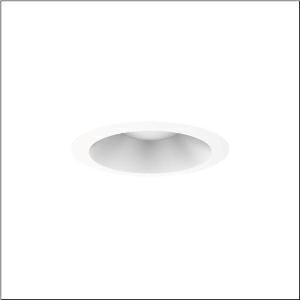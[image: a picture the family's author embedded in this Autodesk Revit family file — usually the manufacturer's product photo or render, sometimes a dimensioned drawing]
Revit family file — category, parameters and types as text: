
# Revit family: lunis_31_midi_51dn16dg32
name_source: partatom
category: Lighting Fixtures
units: mm (PartAtom-declared; Revit-internal decimal feet)

## family parameters
Cut with Voids When Loaded = No
Host = Face
Light Source = No
Part Type = Normal
Room Calculation Point = No
Round Connector Dimension = Use Diameter
Shared = No

## types (1)
- Lunis 31 midi (1 x LED, 2000 lm, 17 W, 3000K)
    Apparent Load = 17 VA
    CIE Flux Codes = 64 93 99 100 100
    Color Rendering = 80
    Color Temperature = 3000K
    Default Elevation = 1800 mm
    Description = Lunis 31,  midi, downlight, light control with reflector, light emission: direct distribution, LED rated luminous flux: 2.000lm, light colour: 830, mains connection: 220..240V, AC, 50/60Hz, housing, white, protection rating (complete): IP20, protection rating (on room side): IP54, insulation class (complete): insulation class II (safety insulation), certification: CE, packaging unit: 1 piece
    Height = 0 mm  [stored 0 ft]
    Lamp = 1 x LED
    Lamp Light Flux = 2000 lm
    Lamp Power = 17 W
    Lamp count = 1
    Length = 259 mm
    Luminous efficacy = 118 lm/W
    Manufacturer = Siteco
    ModVariant = No
    Model = 51DN16DG32
    Mounting Place = Ceiling
    Mounting Type = Recessed
    Number of Poles = 1
    OnlyDefault = Yes
    Power Factor = 1
    Product Name = Lunis 31 midi
    Product group = downlight
    ProductGroupID = 400
    Protection Class = Protection class II
    Protection Degree = IP 20
    RLX_Detail_Level = 1
    RLX_Emergency_Light_Flux = 0 lm
    RLX_Emergency_Type = 0
    RLX_Emergency_Type_DB = No
    RlxData = <blob elided: 23713 chars, md5=bb2857c3>
    Socket = socket
    Standby Power = 0 W
    System Light Flux = 2000 lm
    System Power = 17 W
    Type Comments = Product without accessories
    Type Image = l_1006711.jpg
    URL = http://relux.com
    VarID = ---
    Voltage = 0 V
    Weight = 0.00 kg
    Width = 0 mm  [stored 0 ft]

note: [stored X ft] marks values corroborated as IEEE doubles in the binary element streams (Revit-internal decimal feet)

## geometry (parser evidence)
native form markers: Blend x4, Sweep x10
no freeform markers — native parametric forms only
